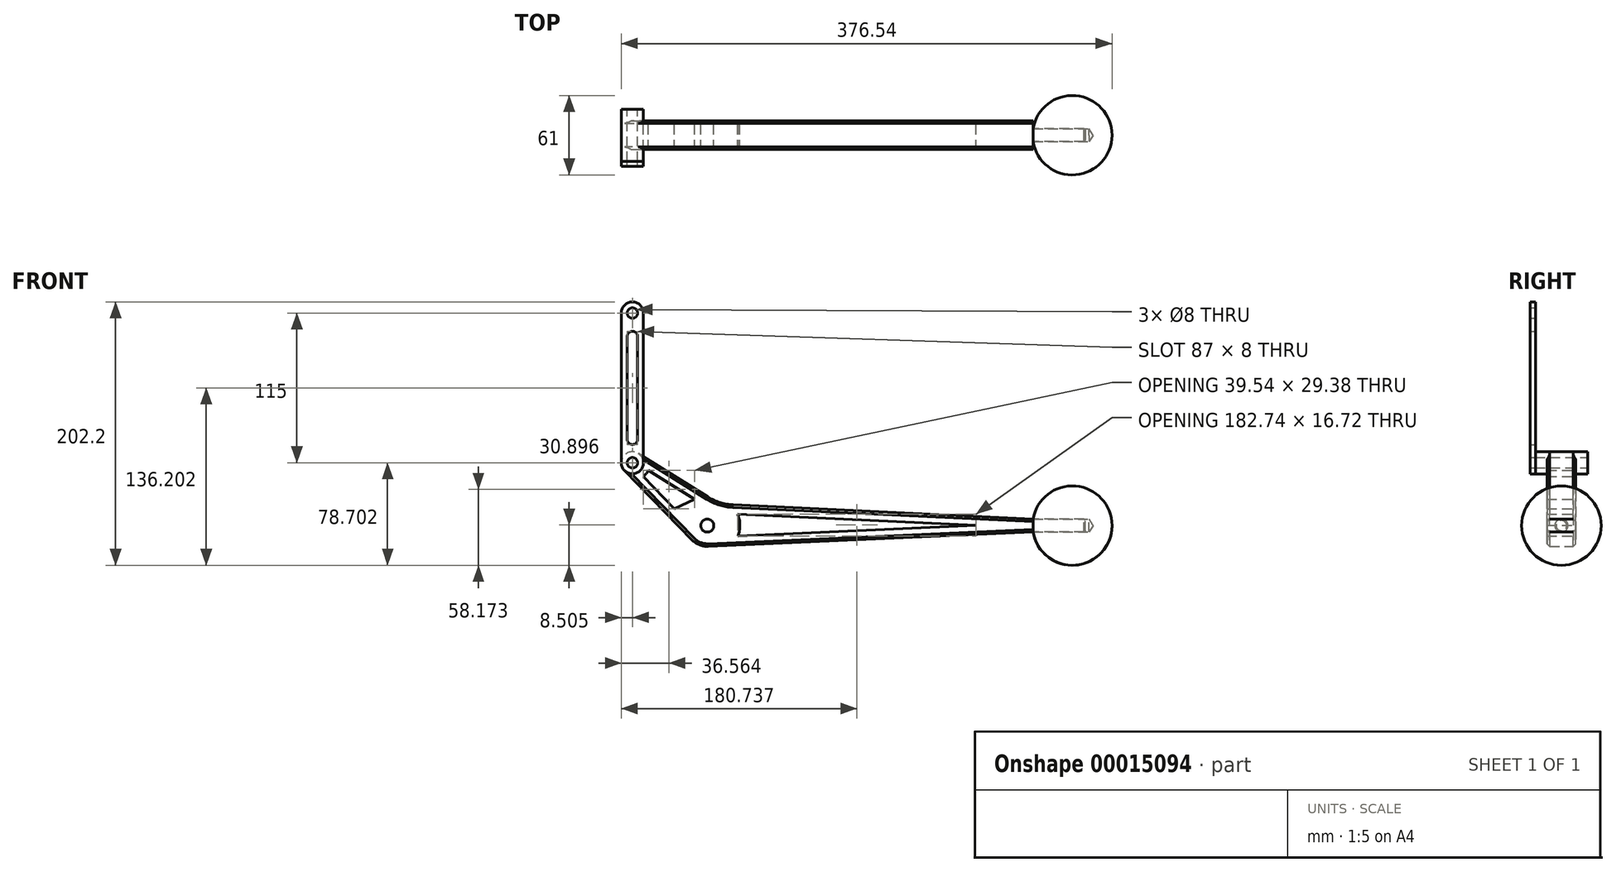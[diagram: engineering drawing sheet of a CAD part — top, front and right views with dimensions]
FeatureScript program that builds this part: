
annotation { "Feature Type Name" : "Feature", "Feature Type Description" : "" }
export const myFeature = defineFeature(function(context is Context, id is Id, definition is map)
    precondition{}
    {
        {
            var Q0;
            Q0=qCreatedBy(makeId("Front.planeOp"),FACE);
            var sketch = newSketch(context, id + "F0", { "sketchPlane" : qUnion([Q0])});
            skCircle(sketch, "E0", {"center": v(0, 0) * mm, "radius": 5 * mm});
            skArc(sketch, "E1", {"start": v(-11.46, -11.17) * mm, "mid": v(-5.9, -14.88) * mm, "end": v(0.7, -15.98) * mm});
            skArc(sketch, "E2", {"start": v(23.7, -7.96) * mm, "mid": v(25, 0.42) * mm, "end": v(23.42, 8.76) * mm});
            skLineSegment(sketch, "E3", {"start": v(0, 0) * mm, "end": v(250, 0) * mm, "construction": true});
            skLineSegment(sketch, "E4", {"start": v(250, 5) * mm, "end": v(250, -5) * mm});
            skLineSegment(sketch, "E5", {"start": v(0, 0) * mm, "end": v(-119.1, 99.94) * mm, "construction": true});
            skCircle(sketch, "E6", {"center": v(-57.45, 48.2) * mm, "radius": 4 * mm});
            skCircle(sketch, "E7", {"center": v(-57.45, 48.2) * mm, "radius": 8.5 * mm});
            skArc(sketch, "E8", {"start": v(-49.16, 37.55) * mm, "mid": v(-46.93, 39.73) * mm, "end": v(-45.27, 42.36) * mm});
            skLineSegment(sketch, "E9", {"start": v(-63.53, 42.27) * mm, "end": v(-11.46, -11.17) * mm});
            skLineSegment(sketch, "E10", {"start": v(0.7, -15.98) * mm, "end": v(250, -5) * mm});
            skLineSegment(sketch, "E11", {"start": v(250, 5) * mm, "end": v(19.88, 15.93) * mm});
            skLineSegment(sketch, "E12", {"start": v(-52.94, 55.41) * mm, "end": v(0.58, 21.97) * mm});
            skPoint(sketch, "E13.visualSharp", {"position": v(9.44, 16.43) * mm});
            skArc(sketch, "E13.filletArc", {"start": v(0.58, 21.97) * mm, "mid": v(9.84, 17.7) * mm, "end": v(19.88, 15.93) * mm});
            skLineSegment(sketch, "E14.0", {"start": v(206.16, 0.08) * mm, "end": v(23.42, 8.76) * mm});
            skLineSegment(sketch, "E15.0", {"start": v(23.7, -7.96) * mm, "end": v(206.16, 0.08) * mm});
            skLineSegment(sketch, "E16.trimOffspring", {"start": v(-45.27, 42.36) * mm, "end": v(-9.62, 20.08) * mm});
            skLineSegment(sketch, "E17.trimOffspring", {"start": v(-49.16, 37.55) * mm, "end": v(-25.22, 12.98) * mm});
            skLineSegment(sketch, "E18", {"start": v(-25.22, 12.98) * mm, "end": v(-9.62, 20.08) * mm});
            skSolve(sketch);
        }
        {
            var Q0;
            Q0=makeQuery(id+"F0.imprint","IMPRINT",FACE,{"disambiguationData":[TD([[makeQuery(id+"F0.imprint","IMPRINT",EDGE,{"derivedFrom":sQuery(id+"F0.wireOp",EDGE,"E0")}),-1.0]])]});
            extrude(context, id + "F1", {"entities" : qUnion([Q0]), "depth" : 11 * mm});
        }
        {
            var Q0;
            Q0=makeQuery(id+"F0.imprint","IMPRINT",FACE,{"disambiguationData":[TD([[makeQuery(id+"F0.imprint","IMPRINT",EDGE,{"derivedFrom":sQuery(id+"F0.wireOp",EDGE,"E6")}),-1.0]])]});
            extrude(context, id + "F2", {"entities" : qUnion([Q0]), "operationType" : NewBodyOperationType.ADD, "depth" : 20 * mm});
        }
        {
            var Q0;
            Q0=makeQuery(id+"F1.opExtrude","SWEPT_BODY",BODY,{"disambiguationData":[OSD([sQuery(id+"F0.wireOp",EDGE,"E0"),sQuery(id+"F0.wireOp",EDGE,"E1"),sQuery(id+"F0.wireOp",EDGE,"E2"),sQuery(id+"F0.wireOp",EDGE,"E4"),sQuery(id+"F0.wireOp",EDGE,"E7"),sQuery(id+"F0.wireOp",EDGE,"E8"),sQuery(id+"F0.wireOp",EDGE,"E9"),sQuery(id+"F0.wireOp",EDGE,"E10"),sQuery(id+"F0.wireOp",EDGE,"E11"),sQuery(id+"F0.wireOp",EDGE,"E12"),sQuery(id+"F0.wireOp",EDGE,"E13.filletArc"),sQuery(id+"F0.wireOp",EDGE,"E14.0"),sQuery(id+"F0.wireOp",EDGE,"E15.0"),sQuery(id+"F0.wireOp",EDGE,"E16.trimOffspring"),sQuery(id+"F0.wireOp",EDGE,"E17.trimOffspring"),sQuery(id+"F0.wireOp",EDGE,"E18")])]});
            var Q1;
            Q1=makeQuery(id+"F0.imprint","IMPRINT",FACE,{"disambiguationData":[TD([[makeQuery(id+"F0.imprint","IMPRINT",EDGE,{"derivedFrom":sQuery(id+"F0.wireOp",EDGE,"E0")}),-1.0]])]});
            mirror(context, id + "F3", {"operationType" : NewBodyOperationType.ADD, "entities" : qUnion([Q0]), "mirrorPlane" : qUnion([Q1])});
        }
        {
            var Q0;
            Q0=makeQuery(id+"F1.opExtrude","CAP_EDGE",EDGE,{"disambiguationData":[OSD([sQuery(id+"F0.wireOp",EDGE,"E11")])],"isStart":false});
            var Q1;
            Q1=makeQuery(id+"F3.opPattern","COPY",EDGE,{"derivedFrom":makeQuery(id+"F1.opExtrude","CAP_EDGE",EDGE,{"disambiguationData":[OSD([sQuery(id+"F0.wireOp",EDGE,"E11")])],"isStart":false}),"instanceName":"1"});
            var Q2;
            Q2=makeQuery(id+"F1.opExtrude","CAP_EDGE",EDGE,{"disambiguationData":[OSD([sQuery(id+"F0.wireOp",EDGE,"E10")])],"isStart":false});
            var Q3;
            Q3=makeQuery(id+"F3.opPattern","COPY",EDGE,{"derivedFrom":makeQuery(id+"F1.opExtrude","CAP_EDGE",EDGE,{"disambiguationData":[OSD([sQuery(id+"F0.wireOp",EDGE,"E10")])],"isStart":false}),"instanceName":"1"});
            chamfer(context, id + "F4", {"entities" : qUnion([Q0, Q1, Q2, Q3]), "width" : 2 * mm, "tangentPropagation" : true});
        }
        {
            var Q0;
            {var subQ0=makeQuery(id+"F1.opExtrude","SWEPT_FACE",FACE,{"disambiguationData":[OSD([sQuery(id+"F0.wireOp",EDGE,"E4")])]});Q0=makeQuery(id+"F3.boolean.opBoolean","MERGE",FACE,{"derivedFrom":[subQ0,makeQuery(id+"F3.opPattern","COPY",FACE,{"derivedFrom":subQ0,"instanceName":"1"})]});}
            var sketch = newSketch(context, id + "F5", { "sketchPlane" : qUnion([Q0])});
            skCircle(sketch, "E19", {"center": v(0, 0) * mm, "radius": 5 * mm});
            skSolve(sketch);
        }
        {
            var Q0;
            {var subQ0=sQuery(id+"F5.wireOp",EDGE,"E19");var subQ1=sQuery(id+"F0.wireOp",EDGE,"E4");var subQ4=makeQuery(id+"F1.opExtrude","SWEPT_EDGE",EDGE,{"disambiguationData":[OSD([subQ1,sQuery(id+"F0.wireOp",EDGE,"E11")])]});var subQ5=makeQuery(id+"F5.imprint","INTERSECT",VERTEX,{"derivedFrom":[makeQuery(id+"F3.boolean.opBoolean","MERGE",EDGE,{"derivedFrom":[subQ4,makeQuery(id+"F3.opPattern","COPY",EDGE,{"derivedFrom":subQ4,"instanceName":"1"})]}),subQ0]});Q0=makeQuery(id+"F5.imprint","IMPRINT",FACE,{"disambiguationData":[TD([[makeQuery(id+"F5.imprint","IMPRINT",EDGE,{"disambiguationData":[TD([[subQ5,-1.0]])],"derivedFrom":subQ0}),1.0]])]});}
            extrude(context, id + "F6", {"entities" : qUnion([Q0]), "operationType" : NewBodyOperationType.ADD, "depth" : 40 * mm});
        }
        {
            var Q0;
            Q0=makeQuery(id+"F6.opExtrude","CAP_EDGE",EDGE,{"disambiguationData":[OSD([sQuery(id+"F5.wireOp",EDGE,"E19")])],"isStart":false});
            chamfer(context, id + "F7", {"entities" : qUnion([Q0]), "width" : 1 * mm, "tangentPropagation" : true});
        }
        {
            var Q0;
            Q0=makeQuery(id+"F2.opExtrude","CAP_FACE",FACE,{"disambiguationData":[OSD([sQuery(id+"F0.wireOp",EDGE,"E6"),sQuery(id+"F0.wireOp",EDGE,"E7")])],"isStart":false});
            var sketch = newSketch(context, id + "F8", { "sketchPlane" : qUnion([Q0])});
            skCircle(sketch, "E20.0", {"center": v(-57.45, 48.2) * mm, "radius": 4 * mm});
            skArc(sketch, "E21", {"start": v(-65.95, 48.2) * mm, "mid": v(-57.45, 39.7) * mm, "end": v(-48.95, 48.2) * mm});
            skLineSegment(sketch, "E22", {"start": v(-57.45, 48.2) * mm, "end": v(-57.45, 163.2) * mm, "construction": true});
            skCircle(sketch, "E23", {"center": v(-57.45, 163.2) * mm, "radius": 4 * mm});
            skArc(sketch, "E24", {"start": v(-48.95, 163.2) * mm, "mid": v(-57.45, 171.7) * mm, "end": v(-65.95, 163.2) * mm});
            skLineSegment(sketch, "E25", {"start": v(-65.95, 48.2) * mm, "end": v(-65.95, 163.2) * mm});
            skLineSegment(sketch, "E26", {"start": v(-48.95, 48.2) * mm, "end": v(-48.95, 163.2) * mm});
            skLineSegment(sketch, "E27", {"start": v(-48.95, 105.7) * mm, "end": v(-65.95, 105.7) * mm, "construction": true});
            skArc(sketch, "E28", {"start": v(-53.45, 145.2) * mm, "mid": v(-57.45, 149.2) * mm, "end": v(-61.45, 145.2) * mm});
            skArc(sketch, "E29", {"start": v(-61.45, 66.2) * mm, "mid": v(-57.45, 62.2) * mm, "end": v(-53.45, 66.2) * mm});
            skLineSegment(sketch, "E30", {"start": v(-61.45, 145.2) * mm, "end": v(-61.45, 66.2) * mm});
            skLineSegment(sketch, "E31", {"start": v(-53.45, 145.2) * mm, "end": v(-53.45, 66.2) * mm});
            skSolve(sketch);
        }
        {
            var Q0;
            Q0=makeQuery(id+"F8.imprint","IMPRINT",FACE,{"disambiguationData":[TD([[makeQuery(id+"F8.imprint","IMPRINT",EDGE,{"derivedFrom":sQuery(id+"F8.wireOp",EDGE,"E23")}),-1.0]])]});
            var Q1;
            Q1=makeQuery(id+"F8.imprint","IMPRINT",FACE,{"disambiguationData":[TD([[makeQuery(id+"F8.imprint","IMPRINT",EDGE,{"derivedFrom":sQuery(id+"F8.wireOp",EDGE,"E20.0")}),-1.0]])]});
            extrude(context, id + "F9", {"entities" : qUnion([Q0, Q1]), "depth" : 4 * mm});
        }
        {
            var Q0;
            Q0=qCreatedBy(makeId("Front.planeOp"),FACE);
            var sketch = newSketch(context, id + "F10", { "sketchPlane" : qUnion([Q0])});
            skLineSegment(sketch, "E32", {"start": v(0, 0) * mm, "end": v(359.46, 0) * mm, "construction": true});
            skLineSegment(sketch, "E33", {"start": v(250, 5) * mm, "end": v(290, 5) * mm});
            skLineSegment(sketch, "E34", {"start": v(289, -5) * mm, "end": v(250, -5) * mm, "construction": true});
            skLineSegment(sketch, "E35.0", {"start": v(250, 3) * mm, "end": v(250, -3) * mm, "construction": true});
            skLineSegment(sketch, "E36.0", {"start": v(290, 5) * mm, "end": v(290, -4) * mm, "construction": true});
            skArc(sketch, "E37", {"start": v(250, -5) * mm, "mid": v(310.59, 0) * mm, "end": v(250, 5) * mm});
            skLineSegment(sketch, "E38", {"start": v(310.59, 0) * mm, "end": v(249.59, 0) * mm});
            skLineSegment(sketch, "E39.0", {"start": v(250, 5) * mm, "end": v(250, 3) * mm});
            skLineSegment(sketch, "E40.0", {"start": v(250, -3) * mm, "end": v(250, -5) * mm});
            skPoint(sketch, "E41.orphan", {"position": v(290, 4) * mm});
            skLineSegment(sketch, "E42", {"start": v(290, 5) * mm, "end": v(293, 5) * mm});
            skLineSegment(sketch, "E43", {"start": v(293, 5) * mm, "end": v(296, 0) * mm});
            skLineSegment(sketch, "E44", {"start": v(296, 0) * mm, "end": v(290, 0) * mm});
            skSolve(sketch);
        }
        {
            var Q0;
            {var subQ4=sQuery(id+"F10.wireOp",EDGE,"E33");Q0=makeQuery(id+"F10.imprint","IMPRINT",FACE,{"disambiguationData":[TD([[makeQuery(id+"F10.imprint","IMPRINT",EDGE,{"derivedFrom":subQ4}),1.0]])]});}
            var Q1;
            Q1=sQuery(id+"F10.wireOp",EDGE,"E38");
            revolve(context, id + "F11", {"entities" : qUnion([Q0]), "axis" : qUnion([Q1]), "revolveType" : RevolveType.FULL});
        }
    });
